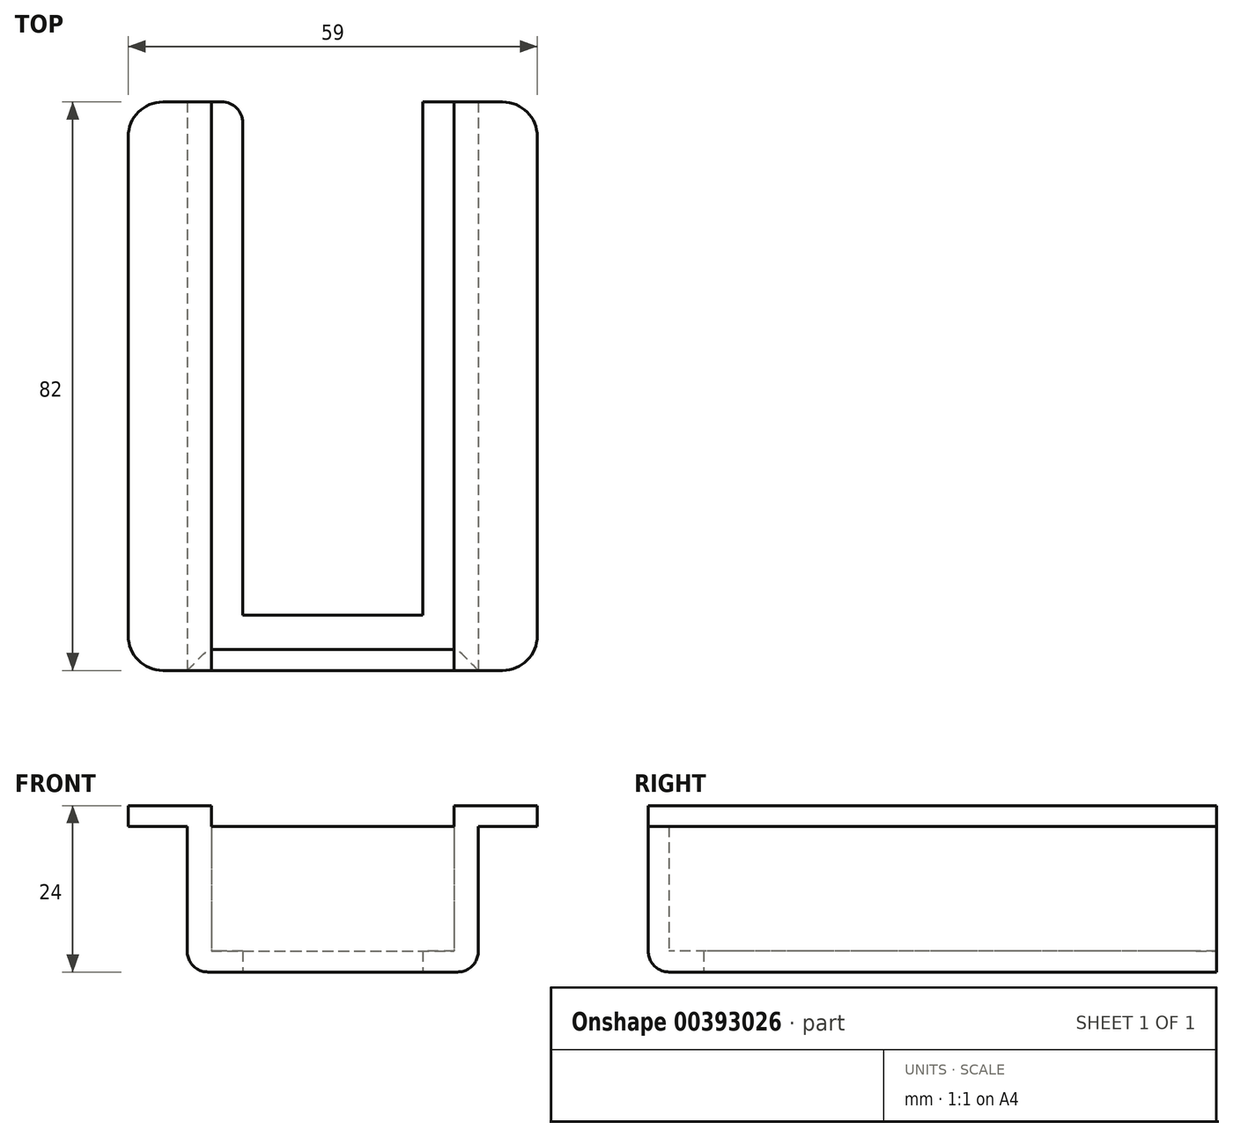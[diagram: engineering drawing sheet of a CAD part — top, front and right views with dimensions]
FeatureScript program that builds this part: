
annotation { "Feature Type Name" : "Feature", "Feature Type Description" : "" }
export const myFeature = defineFeature(function(context is Context, id is Id, definition is map)
    precondition{}
    {
        {
            var Q0;
            Q0=qCreatedBy(makeId("Top.planeOp"),FACE);
            var sketch = newSketch(context, id + "F0", { "sketchPlane" : qUnion([Q0])});
            skLineSegment(sketch, "E0.bottom", {"start": v(-18, 38) * mm, "end": v(18, 38) * mm, "construction": true});
            skLineSegment(sketch, "E0.top", {"start": v(-18, -38) * mm, "end": v(18, -38) * mm, "construction": true});
            skLineSegment(sketch, "E0.left", {"start": v(-18, 38) * mm, "end": v(-18, -38) * mm, "construction": true});
            skLineSegment(sketch, "E0.right", {"start": v(18, 38) * mm, "end": v(18, -38) * mm, "construction": true});
            skPoint(sketch, "E0.middle", {"position": v(0, 0) * mm});
            skLineSegment(sketch, "E1.bottom", {"start": v(-21, 41) * mm, "end": v(21, 41) * mm});
            skLineSegment(sketch, "E1.top", {"start": v(-21, -41) * mm, "end": v(21, -41) * mm});
            skLineSegment(sketch, "E1.left", {"start": v(-21, 41) * mm, "end": v(-21, -41) * mm});
            skLineSegment(sketch, "E1.right", {"start": v(21, 41) * mm, "end": v(21, -41) * mm});
            skSolve(sketch);
        }
        {
            var Q0;
            Q0 = qSketchRegion(id + "F0", true);
            extrude(context, id + "F1", {"entities" : qUnion([Q0]), "depth" : 3 * mm});
        }
        {
            var Q0;
            Q0=makeQuery(id+"F1.opExtrude","CAP_FACE",FACE,{"disambiguationData":[OSD([sQuery(id+"F0.wireOp",EDGE,"E1.bottom"),sQuery(id+"F0.wireOp",EDGE,"E1.top"),sQuery(id+"F0.wireOp",EDGE,"E1.left"),sQuery(id+"F0.wireOp",EDGE,"E1.right")])],"isStart":false});
            var sketch = newSketch(context, id + "F2", { "sketchPlane" : qUnion([Q0])});
            skLineSegment(sketch, "E2.bottom", {"start": v(-17.5, 38) * mm, "end": v(17.5, 38) * mm});
            skLineSegment(sketch, "E2.top", {"start": v(-17.5, -38) * mm, "end": v(17.5, -38) * mm});
            skLineSegment(sketch, "E2.left", {"start": v(-17.5, 38) * mm, "end": v(-17.5, -38) * mm});
            skLineSegment(sketch, "E2.right", {"start": v(17.5, 38) * mm, "end": v(17.5, -38) * mm});
            skPoint(sketch, "E2.middle", {"position": v(0, 0) * mm});
            skSolve(sketch);
        }
        {
            var Q0;
            Q0=makeQuery(id+"F2.imprint","IMPRINT",FACE,{"disambiguationData":[TD([[makeQuery(id+"F2.imprint","IMPRINT",EDGE,{"derivedFrom":sQuery(id+"F2.wireOp",EDGE,"E2.bottom")}),1.0]])]});
            extrude(context, id + "F3", {"entities" : qUnion([Q0]), "operationType" : NewBodyOperationType.ADD, "depth" : 18 * mm});
        }
        {
            var Q0;
            Q0=makeQuery(id+"F3.opExtrude","CAP_FACE",FACE,{"disambiguationData":[OSD([sQuery(id+"F0.wireOp",EDGE,"E1.bottom"),sQuery(id+"F0.wireOp",EDGE,"E1.top"),sQuery(id+"F0.wireOp",EDGE,"E1.left"),sQuery(id+"F0.wireOp",EDGE,"E1.right"),sQuery(id+"F2.wireOp",EDGE,"E2.bottom"),sQuery(id+"F2.wireOp",EDGE,"E2.top"),sQuery(id+"F2.wireOp",EDGE,"E2.left"),sQuery(id+"F2.wireOp",EDGE,"E2.right")])],"isStart":false});
            var sketch = newSketch(context, id + "F4", { "sketchPlane" : qUnion([Q0])});
            skLineSegment(sketch, "E3.bottom", {"start": v(-17.5, -41) * mm, "end": v(-29.5, -41) * mm});
            skLineSegment(sketch, "E3.top", {"start": v(-17.5, 41) * mm, "end": v(-29.5, 41) * mm});
            skLineSegment(sketch, "E3.left", {"start": v(-17.5, -41) * mm, "end": v(-17.5, 41) * mm});
            skLineSegment(sketch, "E3.right", {"start": v(-29.5, -41) * mm, "end": v(-29.5, 41) * mm});
            skLineSegment(sketch, "E4.bottom", {"start": v(17.5, 41) * mm, "end": v(29.5, 41) * mm});
            skLineSegment(sketch, "E4.top", {"start": v(17.5, -41) * mm, "end": v(29.5, -41) * mm});
            skLineSegment(sketch, "E4.left", {"start": v(17.5, 41) * mm, "end": v(17.5, -41) * mm});
            skLineSegment(sketch, "E4.right", {"start": v(29.5, 41) * mm, "end": v(29.5, -41) * mm});
            skSolve(sketch);
        }
        {
            var Q0;
            Q0 = qSketchRegion(id + "F4", true);
            extrude(context, id + "F5", {"entities" : qUnion([Q0]), "operationType" : NewBodyOperationType.ADD, "depth" : 3 * mm});
        }
        {
            var Q0;
            Q0=makeQuery(id+"F1.opExtrude","CAP_FACE",FACE,{"disambiguationData":[OSD([sQuery(id+"F0.wireOp",EDGE,"E1.bottom"),sQuery(id+"F0.wireOp",EDGE,"E1.top"),sQuery(id+"F0.wireOp",EDGE,"E1.left"),sQuery(id+"F0.wireOp",EDGE,"E1.right")])],"isStart":true});
            var sketch = newSketch(context, id + "F6", { "sketchPlane" : qUnion([Q0])});
            skLineSegment(sketch, "E5", {"start": v(3.5, 41) * mm, "end": v(3.5, 33) * mm});
            skLineSegment(sketch, "E6", {"start": v(-21, 14.66) * mm, "end": v(-13, 14.66) * mm});
            skLineSegment(sketch, "E7", {"start": v(21, 7.83) * mm, "end": v(13, 7.83) * mm});
            skLineSegment(sketch, "E8.bottom", {"start": v(13, 33) * mm, "end": v(-13, 33) * mm});
            skLineSegment(sketch, "E8.top", {"start": v(13, -41) * mm, "end": v(-13, -41) * mm});
            skLineSegment(sketch, "E8.left", {"start": v(13, 33) * mm, "end": v(13, -41) * mm});
            skLineSegment(sketch, "E8.right", {"start": v(-13, 33) * mm, "end": v(-13, -41) * mm});
            skSolve(sketch);
        }
        {
            var Q0;
            Q0 = qSketchRegion(id + "F6", true);
            extrude(context, id + "F7", {"entities" : qUnion([Q0]), "operationType" : NewBodyOperationType.REMOVE, "oppositeDirection" : true, "depth" : 25 * mm});
        }
        {
            var Q0;
            {var subQ0=sQuery(id+"F2.wireOp",EDGE,"E2.right");var subQ1=sQuery(id+"F2.wireOp",EDGE,"E2.bottom");Q0=makeQuery(id+"F7.boolean.opBoolean","SPLIT",FACE,{"disambiguationData":[TD([makeQuery(id+"F3.opExtrude","SWEPT_FACE",FACE,{"disambiguationData":[OSD([subQ0])]})])],"derivedFrom":makeQuery(id+"F3.opExtrude","SWEPT_FACE",FACE,{"disambiguationData":[OSD([subQ1])]})});}
            var Q1;
            {var subQ0=sQuery(id+"F2.wireOp",EDGE,"E2.left");var subQ1=sQuery(id+"F2.wireOp",EDGE,"E2.bottom");Q1=makeQuery(id+"F7.boolean.opBoolean","SPLIT",FACE,{"disambiguationData":[TD([makeQuery(id+"F3.opExtrude","SWEPT_FACE",FACE,{"disambiguationData":[OSD([subQ0])]})])],"derivedFrom":makeQuery(id+"F3.opExtrude","SWEPT_FACE",FACE,{"disambiguationData":[OSD([subQ1])]})});}
            extrude(context, id + "F8", {"entities" : qUnion([Q0, Q1]), "operationType" : NewBodyOperationType.REMOVE, "oppositeDirection" : true, "depth" : 25 * mm});
        }
        {
            var Q0;
            Q0=makeQuery(id+"F1.opExtrude","CAP_EDGE",EDGE,{"disambiguationData":[OSD([sQuery(id+"F0.wireOp",EDGE,"E1.left")])],"isStart":true});
            var Q1;
            Q1=makeQuery(id+"F1.opExtrude","CAP_EDGE",EDGE,{"disambiguationData":[OSD([sQuery(id+"F0.wireOp",EDGE,"E1.top")])],"isStart":true});
            var Q2;
            Q2=makeQuery(id+"F1.opExtrude","CAP_EDGE",EDGE,{"disambiguationData":[OSD([sQuery(id+"F0.wireOp",EDGE,"E1.right")])],"isStart":true});
            var Q3;
            Q3=makeQuery(id+"F7.boolean.opBoolean","COPY",EDGE,{"derivedFrom":makeQuery(id+"F7.opExtrude","SWEPT_EDGE",EDGE,{"disambiguationData":[OSD([sQuery(id+"F0.wireOp",EDGE,"E1.bottom"),sQuery(id+"F6.wireOp",EDGE,"E8.top"),sQuery(id+"F6.wireOp",EDGE,"E8.right")])]})});
            var Q4;
            Q4=makeQuery(id+"F7.boolean.opBoolean","COPY",EDGE,{"derivedFrom":makeQuery(id+"F7.opExtrude","SWEPT_EDGE",EDGE,{"disambiguationData":[OSD([sQuery(id+"F0.wireOp",EDGE,"E1.bottom"),sQuery(id+"F6.wireOp",EDGE,"E8.top"),sQuery(id+"F6.wireOp",EDGE,"E8.left")])]})});
            fillet(context, id + "F9", {"entities" : qUnion([Q0, Q1, Q2, Q3, Q4]), "radius" : 3 * mm, "tangentPropagation" : true, "allowEdgeOverflow" : false});
        }
        {
            var Q0;
            Q0=makeQuery(id+"F5.opExtrude","SWEPT_EDGE",EDGE,{"disambiguationData":[OSD([sQuery(id+"F4.wireOp",EDGE,"E4.top"),sQuery(id+"F4.wireOp",EDGE,"E4.right")])]});
            var Q1;
            Q1=makeQuery(id+"F5.opExtrude","SWEPT_EDGE",EDGE,{"disambiguationData":[OSD([sQuery(id+"F4.wireOp",EDGE,"E3.bottom"),sQuery(id+"F4.wireOp",EDGE,"E3.right")])]});
            var Q2;
            Q2=makeQuery(id+"F5.opExtrude","SWEPT_EDGE",EDGE,{"disambiguationData":[OSD([sQuery(id+"F4.wireOp",EDGE,"E3.top"),sQuery(id+"F4.wireOp",EDGE,"E3.right")])]});
            var Q3;
            Q3=makeQuery(id+"F5.opExtrude","SWEPT_EDGE",EDGE,{"disambiguationData":[OSD([sQuery(id+"F4.wireOp",EDGE,"E4.bottom"),sQuery(id+"F4.wireOp",EDGE,"E4.right")])]});
            fillet(context, id + "F10", {"entities" : qUnion([Q0, Q1, Q2, Q3]), "radius" : 5 * mm, "tangentPropagation" : true, "allowEdgeOverflow" : false});
        }
    });
